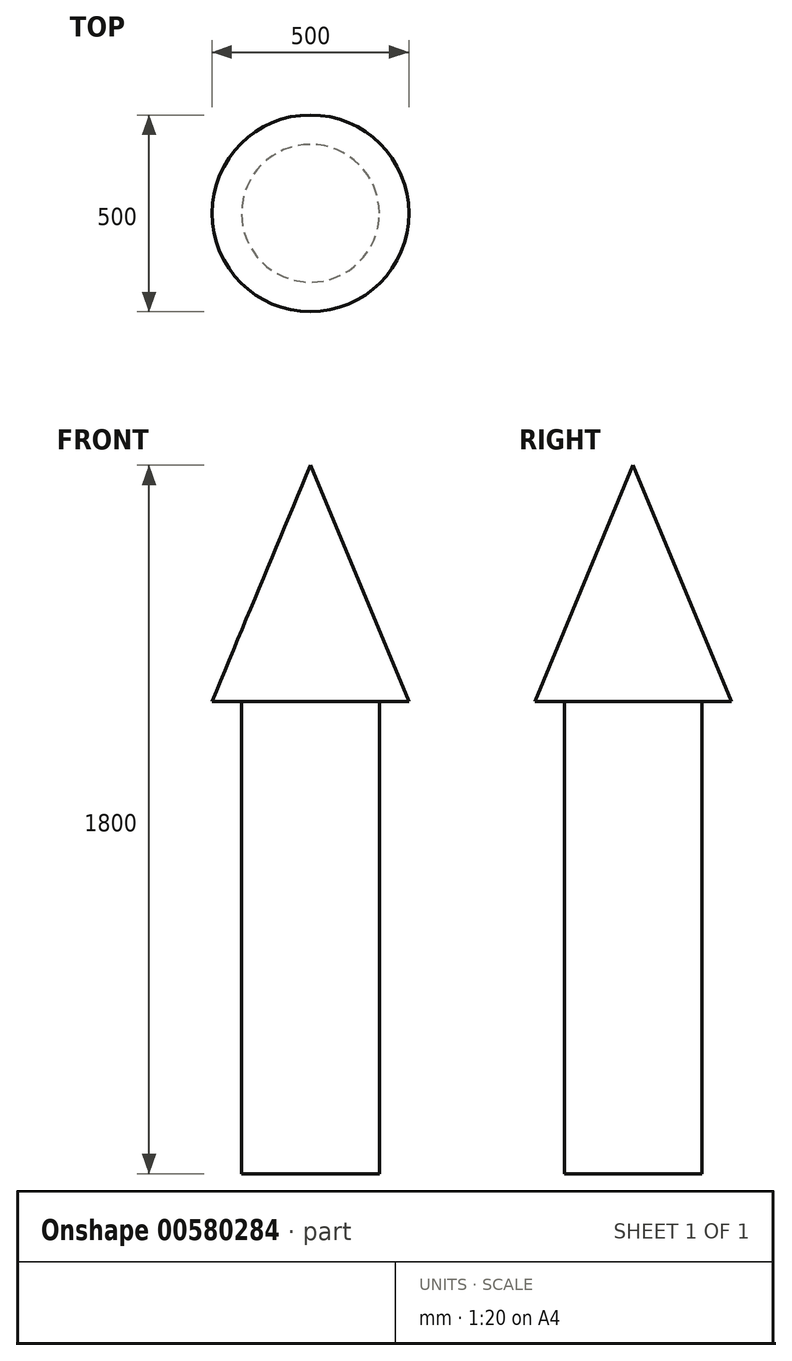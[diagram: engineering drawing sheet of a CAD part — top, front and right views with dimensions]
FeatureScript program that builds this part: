
annotation { "Feature Type Name" : "Feature", "Feature Type Description" : "" }
export const myFeature = defineFeature(function(context is Context, id is Id, definition is map)
    precondition{}
    {
        {
            var Q0;
            Q0=qCreatedBy(makeId("Top.planeOp"),FACE);
            var sketch = newSketch(context, id + "F0", { "sketchPlane" : qUnion([Q0])});
            skCircle(sketch, "E0", {"center": v(0, 0) * mm, "radius": 175 * mm});
            skSolve(sketch);
        }
        {
            var Q0;
            Q0=makeQuery(id+"F0.imprint","IMPRINT",FACE,{"disambiguationData":[TD([[makeQuery(id+"F0.imprint","IMPRINT",EDGE,{"derivedFrom":sQuery(id+"F0.wireOp",EDGE,"E0")}),1.0]])]});
            extrude(context, id + "F1", {"entities" : qUnion([Q0]), "depth" : 1200 * mm, "offsetDistance" : 25 * mm});
        }
        {
            var Q0;
            Q0=qCreatedBy(makeId("Front.planeOp"),FACE);
            var sketch = newSketch(context, id + "F2", { "sketchPlane" : qUnion([Q0])});
            skLineSegment(sketch, "E1", {"start": v(0, 1200) * mm, "end": v(0, 1800) * mm});
            skLineSegment(sketch, "E2", {"start": v(0, 1800) * mm, "end": v(-250, 1200) * mm});
            skLineSegment(sketch, "E3", {"start": v(-250, 1200) * mm, "end": v(0, 1200) * mm});
            skSolve(sketch);
        }
        {
            var Q0;
            Q0=makeQuery(id+"F2.imprint","IMPRINT",FACE,{"disambiguationData":[TD([[makeQuery(id+"F2.imprint","IMPRINT",EDGE,{"derivedFrom":sQuery(id+"F2.wireOp",EDGE,"E1")}),1.0]])]});
            var Q1;
            Q1=sQuery(id+"F2.wireOp",EDGE,"E1");
            revolve(context, id + "F3", {"operationType" : NewBodyOperationType.ADD, "entities" : qUnion([Q0]), "axis" : qUnion([Q1]), "revolveType" : RevolveType.FULL});
        }
    });
